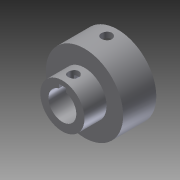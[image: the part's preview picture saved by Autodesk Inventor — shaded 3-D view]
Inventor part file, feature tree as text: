
AUTODESK INVENTOR PART (.ipt)
format: ipt  version: 2012 (Build 160160000, 160)  size: 131,072 bytes
history: native  units: in
note: dims shown in document units (in); Inventor stores cm internally (conversion verified against a paired STEP export)
features: extrude x4, sketch x2
ambient origin geometry x8: Origin, YZ Plane, XZ Plane, XY Plane, X Axis, Y Axis, Z Axis, Center Point
bodies: Solid1 (feature_tree)
feature tree (6):
  sketch  "Sketch1"  dims[d0=0.75in d1=0.875in]
  extrude  "Extrusion1"  Depth=0.875in
  extrude  "Extrusion2"  Depth=0.5in
  extrude  "Extrusion3"  Depth=0.125in TaperAngle=0.0deg
  extrude  "Extrusion4"  Depth=0.375in TaperAngle=0.0deg
  sketch  "Sketch2"  dims[d2=0.315in d3=0.5in d4=0.125in d5=0.0in d6=0.375in d7=0.0in d8=0.25in d9=0.0in d10=0.1181in d11=0.125in d12=0.125in d13=0.375in d14=0.0in d15=0.0787in d16=0.0787in d17=0.0394in d18=0.1969in]
